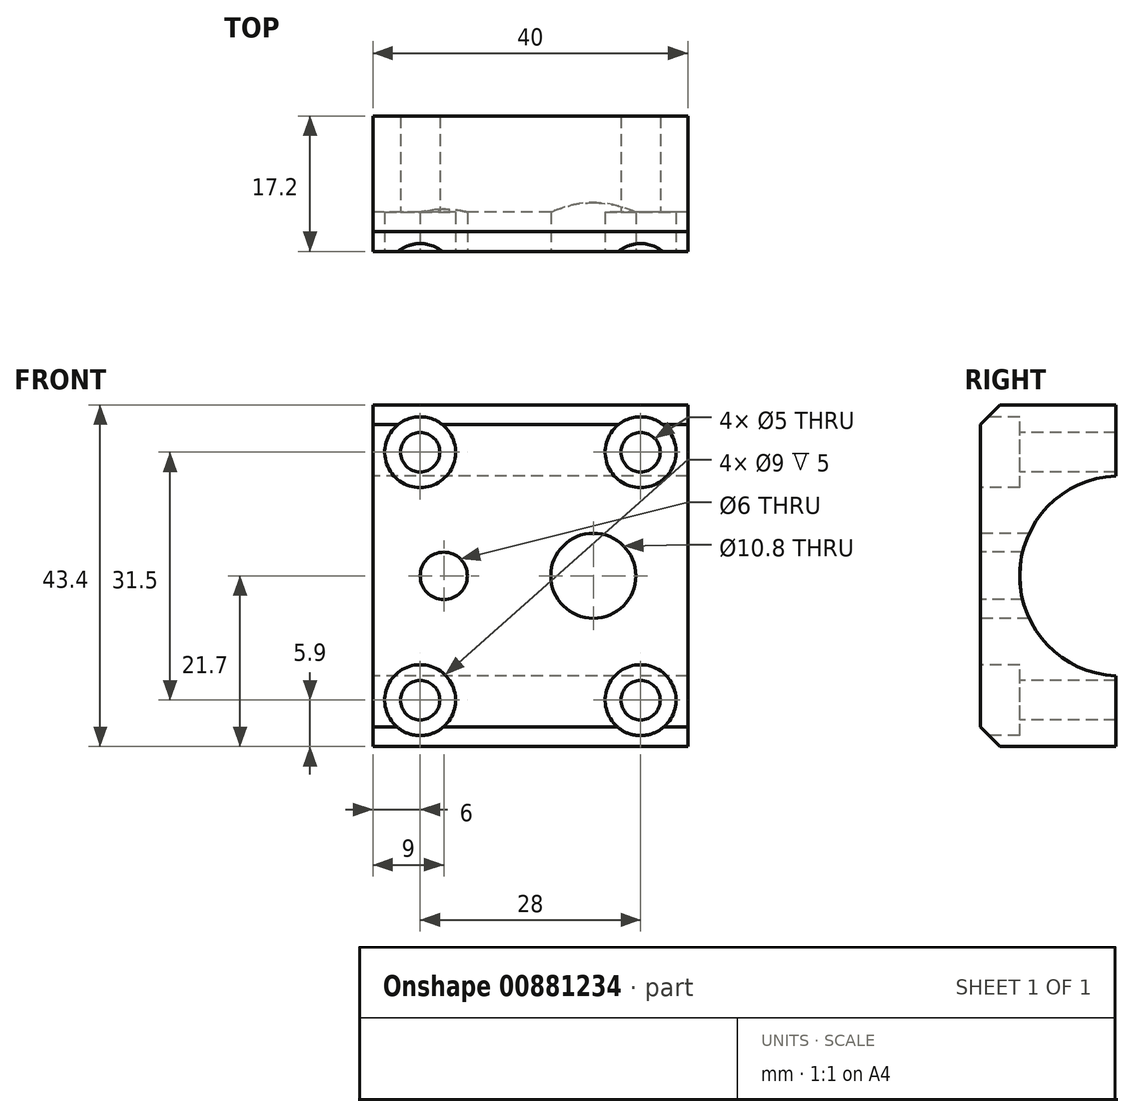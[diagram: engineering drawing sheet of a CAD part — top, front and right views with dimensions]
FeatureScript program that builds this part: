
annotation { "Feature Type Name" : "Feature", "Feature Type Description" : "" }
export const myFeature = defineFeature(function(context is Context, id is Id, definition is map)
    precondition{}
    {
        {
            var Q0;
            Q0=qCreatedBy(makeId("Right.planeOp"),FACE);
            var sketch = newSketch(context, id + "F0", { "sketchPlane" : qUnion([Q0])});
            skArc(sketch, "E0", {"start": v(-0.5, 12.7) * mm, "mid": v(-12.7, 0) * mm, "end": v(-0.5, -12.7) * mm});
            skLineSegment(sketch, "E1.bottom", {"start": v(-17.7, 21.7) * mm, "end": v(-0.5, 21.7) * mm});
            skLineSegment(sketch, "E1.top", {"start": v(-17.7, -21.7) * mm, "end": v(-0.5, -21.7) * mm});
            skLineSegment(sketch, "E1.left", {"start": v(-17.7, 21.7) * mm, "end": v(-17.7, -21.7) * mm});
            skLineSegment(sketch, "E1.right", {"start": v(-0.5, 21.7) * mm, "end": v(-0.5, 12.7) * mm});
            skLineSegment(sketch, "E2.trimOffspring", {"start": v(-0.5, -12.7) * mm, "end": v(-0.5, -21.7) * mm});
            skSolve(sketch);
        }
        {
            var Q0;
            Q0=qSketchRegion(id+"F0",true);
            extrude(context, id + "F1", {"entities" : qUnion([Q0]), "depth" : 40 * mm, "offsetDistance" : 25 * mm});
        }
        {
            var Q0;
            Q0=makeQuery(id+"F1.opExtrude","SWEPT_FACE",FACE,{"disambiguationData":[OSD([sQuery(id+"F0.wireOp",EDGE,"E1.left")])]});
            var sketch = newSketch(context, id + "F2", { "sketchPlane" : qUnion([Q0])});
            skPoint(sketch, "E3", {"position": v(6, 15.7) * mm});
            skPoint(sketch, "E4.0.1.0", {"position": v(6, -15.8) * mm});
            skPoint(sketch, "E4.1.0.0", {"position": v(34, 15.7) * mm});
            skPoint(sketch, "E4.1.1.0", {"position": v(34, -15.8) * mm});
            skLineSegment(sketch, "E4.direction1", {"start": v(6, 15.7) * mm, "end": v(34, 15.7) * mm, "construction": true});
            skLineSegment(sketch, "E4.direction2", {"start": v(6, 15.7) * mm, "end": v(6, -15.8) * mm, "construction": true});
            skSolve(sketch);
        }
        {
            var Q0;
            Q0=sQuery(id+"F2.wireOp",VERTEX,"E3");
            var Q1;
            Q1=sQuery(id+"F2.wireOp",VERTEX,"E4.1.0.0");
            var Q2;
            Q2=sQuery(id+"F2.wireOp",VERTEX,"E4.1.1.0");
            var Q3;
            Q3=sQuery(id+"F2.wireOp",VERTEX,"E4.0.1.0");
            var Q4;
            Q4=makeQuery(id+"F1.opExtrude","SWEPT_BODY",BODY,{"disambiguationData":[OSD([sQuery(id+"F0.wireOp",EDGE,"E0"),sQuery(id+"F0.wireOp",EDGE,"E1.bottom"),sQuery(id+"F0.wireOp",EDGE,"E1.top"),sQuery(id+"F0.wireOp",EDGE,"E1.left"),sQuery(id+"F0.wireOp",EDGE,"E1.right"),sQuery(id+"F0.wireOp",EDGE,"E2.trimOffspring")])]});
            hole(context, id + "F3", {"style" : HoleStyle.C_BORE, "endStyle" : HoleEndStyle.THROUGH, "standardTappedOrClearance" : lookupTablePath({ "standard" : "ISO", "size" : "5", "type" : "Drilled" }), "standardBlindInLast" : lookupTablePath({ "standard" : "ISO", "size" : "5", "type" : "Drilled" }), "holeDiameter" : 5 * mm, "cBoreDiameter" : 9 * mm, "cBoreDepth" : 5 * mm, "majorDiameter" : 5 * mm, "isTappedThrough" : true, "tappedDepth" : 12 * mm, "tapClearance" : 3, "startFromSketch" : true, "locations" : qUnion([Q0, Q1, Q2, Q3]), "scope" : qUnion([Q4])});
        }
        {
            var Q0;
            Q0=makeQuery(id+"F1.opExtrude","SWEPT_EDGE",EDGE,{"disambiguationData":[OSD([sQuery(id+"F0.wireOp",EDGE,"E1.bottom"),sQuery(id+"F0.wireOp",EDGE,"E1.left")])]});
            var Q1;
            Q1=makeQuery(id+"F1.opExtrude","SWEPT_EDGE",EDGE,{"disambiguationData":[OSD([sQuery(id+"F0.wireOp",EDGE,"E1.top"),sQuery(id+"F0.wireOp",EDGE,"E1.left")])]});
            chamfer(context, id + "F4", {"entities" : qUnion([Q0, Q1]), "width" : 2.5 * mm, "tangentPropagation" : true});
        }
        {
            var Q0;
            Q0=makeQuery(id+"F1.opExtrude","SWEPT_FACE",FACE,{"disambiguationData":[OSD([sQuery(id+"F0.wireOp",EDGE,"E1.left")])]});
            var sketch = newSketch(context, id + "F5", { "sketchPlane" : qUnion([Q0])});
            skCircle(sketch, "E5", {"center": v(9, 0) * mm, "radius": 3 * mm});
            skSolve(sketch);
        }
        {
            var Q0;
            Q0=qSketchRegion(id+"F5",true);
            extrude(context, id + "F6", {"entities" : qUnion([Q0]), "operationType" : NewBodyOperationType.REMOVE, "endBound" : BoundingType.THROUGH_ALL, "oppositeDirection" : true, "depth" : 25 * mm, "offsetDistance" : 25 * mm});
        }
        {
            var Q0;
            Q0=makeQuery(id+"F1.opExtrude","SWEPT_FACE",FACE,{"disambiguationData":[OSD([sQuery(id+"F0.wireOp",EDGE,"E1.left")])]});
            var sketch = newSketch(context, id + "F7", { "sketchPlane" : qUnion([Q0])});
            skPoint(sketch, "E6", {"position": v(28, 0) * mm});
            skSolve(sketch);
        }
        {
            var Q0;
            Q0=sQuery(id+"F7.wireOp",VERTEX,"E6");
            var Q1;
            Q1=makeQuery(id+"F1.opExtrude","SWEPT_BODY",BODY,{"disambiguationData":[OSD([sQuery(id+"F0.wireOp",EDGE,"E0"),sQuery(id+"F0.wireOp",EDGE,"E1.bottom"),sQuery(id+"F0.wireOp",EDGE,"E1.top"),sQuery(id+"F0.wireOp",EDGE,"E1.left"),sQuery(id+"F0.wireOp",EDGE,"E1.right"),sQuery(id+"F0.wireOp",EDGE,"E2.trimOffspring")])]});
            hole(context, id + "F8", {"style" : HoleStyle.SIMPLE, "endStyle" : HoleEndStyle.BLIND, "standardTappedOrClearance" : lookupTablePath({ "standard" : "ISO", "engagement" : "75%", "pitch" : "1.25 mm", "size" : "M12", "type" : "Tapped" }), "standardBlindInLast" : lookupTablePath({ "standard" : "ISO", "engagement" : "75%", "pitch" : "1.25 mm", "size" : "M12", "type" : "Tapped" }), "holeDiameter" : 10.8 * mm, "majorDiameter" : 12 * mm, "showTappedDepth" : true, "holeDepth" : 11.35 * mm, "tappedDepth" : 7.6 * mm, "tapClearance" : 3, "startFromSketch" : true, "locations" : qUnion([Q0]), "scope" : qUnion([Q1])});
        }
    });
